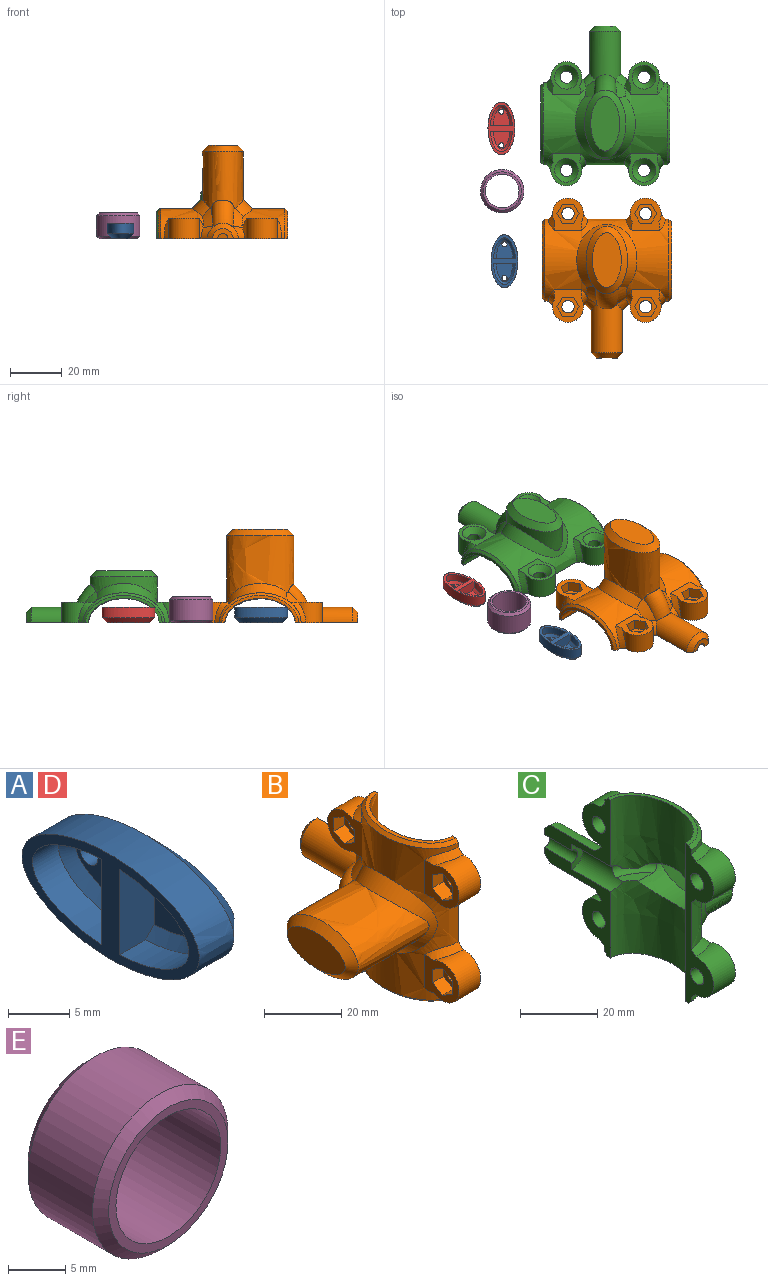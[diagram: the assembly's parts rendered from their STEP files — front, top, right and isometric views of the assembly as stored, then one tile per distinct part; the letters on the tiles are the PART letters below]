
ASSEMBLY  parts=5 mates=4
PART A: 14 faces, bbox 8.8x23.2x13.2 mm
  f0: plane 7.18x6.72mm, normal (-1,0,0), area 31.3mm2, adj f3,f6,f12
  f1: plane 7.18x6.72mm, normal (-1,0,0), area 31.1mm2, adj f2,f9,f11
  f2: cylinder r=1mm len=2mm, axis (1,0,0), area 12.6mm2, adj f1,f5
  f3: cylinder r=1mm len=2mm, axis (1,0,0), area 12.6mm2, adj f0,f5
  f4: extruded ~20.4x10.4mm, area 198.4mm2, adj f10,f13
  f5: plane 16.57x6.56mm, normal (1,0,0), area 75.2mm2, adj f2,f3,f13
  f6: plane 8.55x4mm, normal (0,1,0), area 33.2mm2, adj f0,f8,f10,f12
  f7: extruded ~8.55x8mm, area 58.6mm2, adj f9,f10,f11
  f8: extruded ~8.55x8mm, area 58.6mm2, adj f6,f10,f12
  f9: plane 8.55x4mm, normal (0,-1,0), area 33.2mm2, adj f1,f7,f10,f11
  f10: plane 23.19x13.19mm, normal (-1,0,0), area 61.7mm2, adj f4,f6,f7,f8,f9
  f11: bspline ~8.88x8.6mm, area 25.4mm2, adj f1,f7,f9
  f12: bspline ~8.88x8.6mm, area 25.4mm2, adj f0,f6,f8
  f13: bspline ~20.41x10.4mm, area 122.5mm2, adj f4,f5
PART B: 78 faces, bbox 43.1x63.8x52 mm
  f0: cylinder r=2.4mm len=4.8mm, axis (-1,0,0), area 60.3mm2, adj f71,f76
  f1: cylinder r=2.4mm len=4.8mm, axis (-1,0,0), area 60.3mm2, adj f64,f75
  f2: cylinder r=2.4mm len=4.8mm, axis (-1,0,0), area 60.3mm2, adj f57,f77
  f3: cylinder r=2.4mm len=4.8mm, axis (-1,0,0), area 60.3mm2, adj f50,f77
  f4: bspline ~10.9x9.25mm, area 20.1mm2, adj f8,f21,f29,f41,f75
  f5: bspline ~10.9x9.25mm, area 23.8mm2, adj f8,f20,f40,f76
  f6: bspline ~15.08x7.26mm, area 23.8mm2, adj f8,f22,f42,f77
  f7: bspline ~15.08x7.26mm, area 23.8mm2, adj f8,f23,f43,f77
  f8: extruded ~48x31.6mm, area 880.1mm2, adj f4,f5,f6,f7,f18,f19,f24,f25
  f9: extruded ~50x27.3mm, area 1597.6mm2, adj f11,f12,f15,f33,f35,f36,f75,f76
  f10: cylinder r=2mm len=10mm, axis (0,-1,0), area 62.8mm2, adj f13,f16,f75,f76
  f11: plane 31.64x12.74mm, normal (0,0,1), area 43.5mm2, adj f9,f19,f76,f77
  f12: plane 31.64x12.74mm, normal (0,0,-1), area 43.5mm2, adj f9,f18,f75,f77
  f13: plane 8x4mm, normal (0,1,0), area 18.8mm2, adj f10,f17,f75,f76
  f14: cylinder r=6mm len=18.82mm, axis (0,-1,0), area 341.8mm2, adj f17,f28,f29,f32,f75,f76
  f15: cylinder r=4mm len=15.1mm, axis (0,-1,0), area 169.8mm2, adj f9,f16,f33,f34,f35,f75,f76
  f16: plane 8x4mm, normal (0,-1,0), area 18.8mm2, adj f10,f15,f75,f76
  f17: cone r=6mm half-angle=45deg, axis (0,-1,0), area 44.4mm2, adj f13,f14,f75,f76
  f18: bspline ~31.6x15.29mm, area 59mm2, adj f8,f12,f75,f77
  f19: bspline ~31.6x12.57mm, area 59mm2, adj f8,f11,f76,f77
  f20: cylinder r=6mm len=12mm, axis (-1,0,0), area 181.5mm2, adj f5,f26,f40,f76
  f21: cylinder r=6mm len=12mm, axis (-1,0,0), area 181.5mm2, adj f4,f27,f41,f75
  f22: cylinder r=6mm len=12mm, axis (-1,0,0), area 181.5mm2, adj f6,f25,f42,f77
  f23: cylinder r=6mm len=12mm, axis (-1,0,0), area 181.5mm2, adj f7,f24,f43,f77
  f24: bspline ~9.3x6.12mm, area 23.8mm2, adj f8,f23,f43,f77
  f25: bspline ~9.3x6.12mm, area 23.8mm2, adj f8,f22,f42,f77
  f26: bspline ~9.29x6.11mm, area 20.1mm2, adj f8,f20,f28,f40,f76
  f27: bspline ~9.29x6.11mm, area 23.8mm2, adj f8,f21,f41,f75
  f28: bspline ~6.31x6.22mm, area 21.7mm2, adj f8,f14,f26,f32,f72,f76
  f29: bspline ~7.95x6.22mm, area 21.7mm2, adj f4,f8,f14,f32,f74,f75
  f30: extruded ~26x25.88mm, area 1375.5mm2, adj f32,f39,f72,f73,f74
  f31: plane 21.38x11.38mm, normal (-1,0,0), area 185.7mm2, adj f39
  f32: torus R=15.4mm, axis (0,0,1), area 117.6mm2, adj f14,f28,f29,f30,f72,f74
  f33: plane 8.47x5.25mm, normal (0,0,-1), area 21.6mm2, adj f9,f15,f34,f36
  f34: torus R=15.4mm, axis (0,0,1), area 71.5mm2, adj f15,f33,f35,f36
  f35: plane 8.47x5.25mm, normal (0,0,1), area 21.6mm2, adj f9,f15,f34,f36
  f36: extruded ~25.44x21.2mm, area 1191.9mm2, adj f9,f33,f34,f35,f38
  f37: plane 16.61x6.56mm, normal (1,0,0), area 81.5mm2, adj f38
  f38: bspline ~21.21x11.2mm, area 151.3mm2, adj f36,f37
  f39: bspline ~26.01x16mm, area 201.7mm2, adj f30,f31
  f40: plane 12.88x12.27mm, normal (-1,0,0), area 81.1mm2, adj f5,f8,f20,f26,f65,f66,f67,f68
  f41: plane 12.88x12.27mm, normal (-1,0,0), area 81.1mm2, adj f4,f8,f21,f27,f58,f59,f60,f61
  f42: plane 12.87x12.26mm, normal (-1,0,0), area 81.1mm2, adj f6,f8,f22,f25,f51,f52,f53,f54
  f43: plane 12.87x12.26mm, normal (-1,0,0), area 81.1mm2, adj f7,f8,f23,f24,f44,f45,f46,f47
  f44: plane 4x3.7mm, normal (0,-0.5,-0.87), area 17.1mm2, adj f43,f45,f49,f50
  f45: plane 4.27x4mm, normal (0,-1,0), area 17.1mm2, adj f43,f44,f46,f50
  f46: plane 4x3.7mm, normal (0,-0.5,0.87), area 17.1mm2, adj f43,f45,f47,f50
  f47: plane 4x3.7mm, normal (0,0.5,0.87), area 17.1mm2, adj f43,f46,f48,f50
  f48: plane 4.27x4mm, normal (0,1,0), area 17.1mm2, adj f43,f47,f49,f50
  f49: plane 4x3.7mm, normal (0,0.5,-0.87), area 17.1mm2, adj f43,f44,f48,f50
  f50: plane 8.54x7.4mm, normal (-1,0,0), area 29.3mm2, adj f3,f44,f45,f46,f47,f48,f49
  f51: plane 4x3.7mm, normal (0,-0.5,-0.87), area 17.1mm2, adj f42,f52,f56,f57
  f52: plane 4.27x4mm, normal (0,-1,0), area 17.1mm2, adj f42,f51,f53,f57
  f53: plane 4x3.7mm, normal (0,-0.5,0.87), area 17.1mm2, adj f42,f52,f54,f57
  f54: plane 4x3.7mm, normal (0,0.5,0.87), area 17.1mm2, adj f42,f53,f55,f57
  f55: plane 4.27x4mm, normal (0,1,0), area 17.1mm2, adj f42,f54,f56,f57
  f56: plane 4x3.7mm, normal (0,0.5,-0.87), area 17.1mm2, adj f42,f51,f55,f57
  f57: plane 8.54x7.4mm, normal (-1,0,0), area 29.3mm2, adj f2,f51,f52,f53,f54,f55,f56
  f58: plane 4x3.7mm, normal (0,-0.5,-0.87), area 17.1mm2, adj f41,f59,f63,f64
  f59: plane 4.27x4mm, normal (0,-1,0), area 17.1mm2, adj f41,f58,f60,f64
  f60: plane 4x3.7mm, normal (0,-0.5,0.87), area 17.1mm2, adj f41,f59,f61,f64
  f61: plane 4x3.7mm, normal (0,0.5,0.87), area 17.1mm2, adj f41,f60,f62,f64
  f62: plane 4.27x4mm, normal (0,1,0), area 17.1mm2, adj f41,f61,f63,f64
  f63: plane 4x3.7mm, normal (0,0.5,-0.87), area 17.1mm2, adj f41,f58,f62,f64
  f64: plane 8.54x7.4mm, normal (-1,0,0), area 29.3mm2, adj f1,f58,f59,f60,f61,f62,f63
  f65: plane 4x3.7mm, normal (0,-0.5,-0.87), area 17.1mm2, adj f40,f66,f70,f71
  f66: plane 4.27x4mm, normal (0,-1,0), area 17.1mm2, adj f40,f65,f67,f71
  f67: plane 4x3.7mm, normal (0,-0.5,0.87), area 17.1mm2, adj f40,f66,f68,f71
  f68: plane 4x3.7mm, normal (0,0.5,0.87), area 17.1mm2, adj f40,f67,f69,f71
  f69: plane 4.27x4mm, normal (0,1,0), area 17.1mm2, adj f40,f68,f70,f71
  f70: plane 4x3.7mm, normal (0,0.5,-0.87), area 17.1mm2, adj f40,f65,f69,f71
  f71: plane 8.54x7.4mm, normal (-1,0,0), area 29.3mm2, adj f0,f65,f66,f67,f68,f69,f70
  f72: bspline ~9.11x7.87mm, area 34.1mm2, adj f8,f28,f30,f32,f73
  f73: bspline ~24.16x23.24mm, area 277.6mm2, adj f8,f30,f72,f74
  f74: bspline ~9.1x7.85mm, area 34.1mm2, adj f8,f29,f30,f32,f73
  f75: plane 24.15x23mm, normal (1,0,0), area 179.6mm2, adj f1,f4,f8,f9,f10,f12,f13,f14
  f76: plane 24.15x23mm, normal (1,0,0), area 179.6mm2, adj f0,f5,f8,f9,f10,f11,f13,f14
  f77: plane 50x10.35mm, normal (1,0,0), area 241.8mm2, adj f2,f3,f6,f7,f8,f9,f11,f12
PART C: 54 faces, bbox 26.5x63.8x52 mm
  f0: plane 21.38x11.38mm, normal (1,0,0), area 185.6mm2, adj f2
  f1: plane 16.61x6.56mm, normal (-1,0,0), area 81.4mm2, adj f3
  f2: bspline ~26.01x16mm, area 201.6mm2, adj f0,f4
  f3: bspline ~21.21x11.2mm, area 152.8mm2, adj f1,f6
  f4: extruded ~26x16mm, area 305mm2, adj f2,f5,f14,f15,f16
  f5: bspline ~25.27x23.38mm, area 277.6mm2, adj f4,f14,f15,f38
  f6: extruded ~21.2x11.2mm, area 358mm2, adj f3,f7,f8,f9,f37
  f7: plane 8.47x5.25mm, normal (0,0,-1), area 21.6mm2, adj f6,f8,f33,f37
  f8: torus R=15.4mm, axis (0,0,1), area 71.5mm2, adj f6,f7,f9,f33
  f9: plane 8.48x5.26mm, normal (0,0,1), area 21.6mm2, adj f6,f8,f33,f37
  f10: plane 12.88x12.27mm, normal (1,0,0), area 62.1mm2, adj f19,f20,f38,f39,f43
  f11: plane 12.88x12.27mm, normal (1,0,0), area 62.1mm2, adj f17,f18,f38,f40,f45
  f12: plane 12.88x12.27mm, normal (1,0,0), area 62.1mm2, adj f28,f29,f38,f41,f49
  f13: plane 12.88x12.27mm, normal (1,0,0), area 62.1mm2, adj f21,f22,f38,f42,f47
  f14: bspline ~9.11x7.87mm, area 34.1mm2, adj f4,f5,f16,f27,f38
  f15: bspline ~9.1x7.85mm, area 34.1mm2, adj f4,f5,f16,f26,f38
  f16: torus R=15.4mm, axis (0,0,1), area 117.6mm2, adj f4,f14,f15,f26,f27,f30
  f17: bspline ~9.29x6.11mm, area 23.8mm2, adj f11,f18,f38,f53
  f18: cylinder r=6mm len=12mm, axis (-1,0,0), area 181.5mm2, adj f11,f17,f40,f53
  f19: bspline ~9.29x6.11mm, area 23.8mm2, adj f10,f20,f38,f53
  f20: cylinder r=6mm len=12mm, axis (-1,0,0), area 181.5mm2, adj f10,f19,f39,f53
  f21: bspline ~9.3x6.12mm, area 23.8mm2, adj f13,f22,f38,f51
  f22: cylinder r=6mm len=12mm, axis (-1,0,0), area 181.5mm2, adj f13,f21,f42,f51
  f23: bspline ~31.6x12.57mm, area 59mm2, adj f24,f38,f51,f53
  f24: plane 31.65x12.75mm, normal (0,0,-1), area 43.7mm2, adj f23,f37,f51,f53
  f25: cone r=6mm half-angle=45deg, axis (0,-1,0), area 44.4mm2, adj f30,f31,f51,f52
  f26: bspline ~6.29x6.22mm, area 21.7mm2, adj f15,f16,f30,f38,f42,f51
  f27: bspline ~9.94x6.22mm, area 21.7mm2, adj f14,f16,f28,f30,f38,f52
  f28: bspline ~9.3x6.12mm, area 20.1mm2, adj f12,f27,f29,f38,f52
  f29: cylinder r=6mm len=12mm, axis (-1,0,0), area 181.5mm2, adj f12,f28,f41,f52
  f30: cylinder r=6mm len=18.82mm, axis (0,-1,0), area 341.8mm2, adj f16,f25,f26,f27,f51,f52
  f31: plane 8x4mm, normal (0,1,0), area 18.8mm2, adj f25,f34,f51,f52
  f32: plane 8x4mm, normal (0,-1,0), area 18.8mm2, adj f33,f34,f51,f52
  f33: cylinder r=4mm len=15.1mm, axis (0,-1,0), area 169.8mm2, adj f7,f8,f9,f32,f37,f51,f52
  f34: cylinder r=2mm len=10mm, axis (0,-1,0), area 62.8mm2, adj f31,f32,f51,f52
  f35: bspline ~31.6x15.29mm, area 59mm2, adj f36,f38,f52,f53
  f36: plane 31.65x12.75mm, normal (0,0,1), area 43.7mm2, adj f35,f37,f52,f53
  f37: extruded ~50x27.3mm, area 1597.6mm2, adj f6,f7,f9,f24,f33,f36,f51,f52
  f38: extruded ~48x31.6mm, area 878.4mm2, adj f5,f10,f11,f12,f13,f14,f15,f17
  f39: bspline ~10.92x9.27mm, area 23.8mm2, adj f10,f20,f38,f53
  f40: bspline ~10.92x9.27mm, area 23.8mm2, adj f11,f18,f38,f53
  f41: bspline ~10.91x9.28mm, area 23.8mm2, adj f12,f29,f38,f52
  f42: bspline ~10.91x9.28mm, area 20.1mm2, adj f13,f22,f26,f38,f51
  f43: cone r=2.4mm half-angle=45deg, axis (1,0,0), area 68.4mm2, adj f10,f44
  f44: cylinder r=2.4mm len=5.8mm, axis (-1,0,0), area 87.5mm2, adj f43,f53
  f45: cone r=2.4mm half-angle=45deg, axis (1,0,0), area 68.4mm2, adj f11,f46
  f46: cylinder r=2.4mm len=5.8mm, axis (-1,0,0), area 87.5mm2, adj f45,f53
  f47: cone r=2.4mm half-angle=45deg, axis (1,0,0), area 68.4mm2, adj f13,f48
  f48: cylinder r=2.4mm len=5.8mm, axis (-1,0,0), area 87.5mm2, adj f47,f51
  f49: cone r=2.4mm half-angle=45deg, axis (1,0,0), area 68.4mm2, adj f12,f50
  f50: cylinder r=2.4mm len=5.8mm, axis (-1,0,0), area 87.5mm2, adj f49,f52
  f51: plane 24.15x23mm, normal (-1,0,0), area 179.6mm2, adj f21,f22,f23,f24,f25,f26,f30,f31
  f52: plane 24.15x23mm, normal (-1,0,0), area 179.6mm2, adj f25,f27,f28,f29,f30,f31,f32,f33
  f53: plane 50x10.35mm, normal (-1,0,0), area 241.8mm2, adj f17,f18,f19,f20,f23,f24,f35,f36
PART D: same geometry as A
PART E: 6 faces, bbox 16.8x10x16.8 mm
  f0: cylinder r=6.5mm len=13mm, axis (0,1,0), area 408.4mm2, adj f2,f3
  f1: cylinder r=8.4mm len=16.8mm, axis (0,1,0), area 422.2mm2, adj f4,f5
  f2: plane 14.8x14.8mm, normal (0,-1,0), area 39.3mm2, adj f0,f4
  f3: plane 14.8x14.8mm, normal (0,1,0), area 39.3mm2, adj f0,f5
  f4: cone r=7.4mm half-angle=45deg, axis (0,1,0), area 70.2mm2, adj f1,f2
  f5: cone r=8.4mm half-angle=45deg, axis (0,-1,0), area 70.2mm2, adj f1,f3
PLACE A rot(axis=(-0.71,0,0.71),180deg) t=(-15.18,-26.89,72.91)mm
PLACE B rot(axis=(0.71,0,-0.71),180deg) t=(24.39,-26.51,22.91)mm
PLACE C rot(axis=(0,-1,0),90deg) t=(23.77,26.23,22.91)mm
PLACE D rot(axis=(-0.71,0,0.71),180deg) t=(-16.36,24.43,72.91)mm
PLACE E rot(axis=(-1,0,0),90deg) t=(-16.06,0.2,82.91)mm
MATE planar D.f5 <-> E.f0  axis (0,0,-1) through (-16.37,24.43,22.91)mm
MATE planar B.f3 <-> C.f20  axis (0,0,-1) through (9.39,-8.51,22.91)mm
MATE planar D.f5 <-> C.f29  axis (0,0,-1) through (-16.37,24.43,22.91)mm
MATE planar A.f5 <-> D.f5  axis (0,0,-1) through (-15.18,-26.89,22.91)mm
